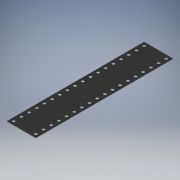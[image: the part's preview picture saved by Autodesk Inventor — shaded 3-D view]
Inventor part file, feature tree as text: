
AUTODESK INVENTOR PART (.ipt)
format: ipt  version: 2019 (Build 230136000, 136)  size: 152,064 bytes
history: native  units: mm
features: extrude x1, other x1
ambient origin geometry x8: Origin, YZ Plane, XZ Plane, XY Plane, X Axis, Y Axis, Z Axis, Center Point
bodies: Solid1 (feature_tree)
feature tree (2):
  extrude  "Foam Body"  Depth=894.0mm
  other  "Foam Scheme"
